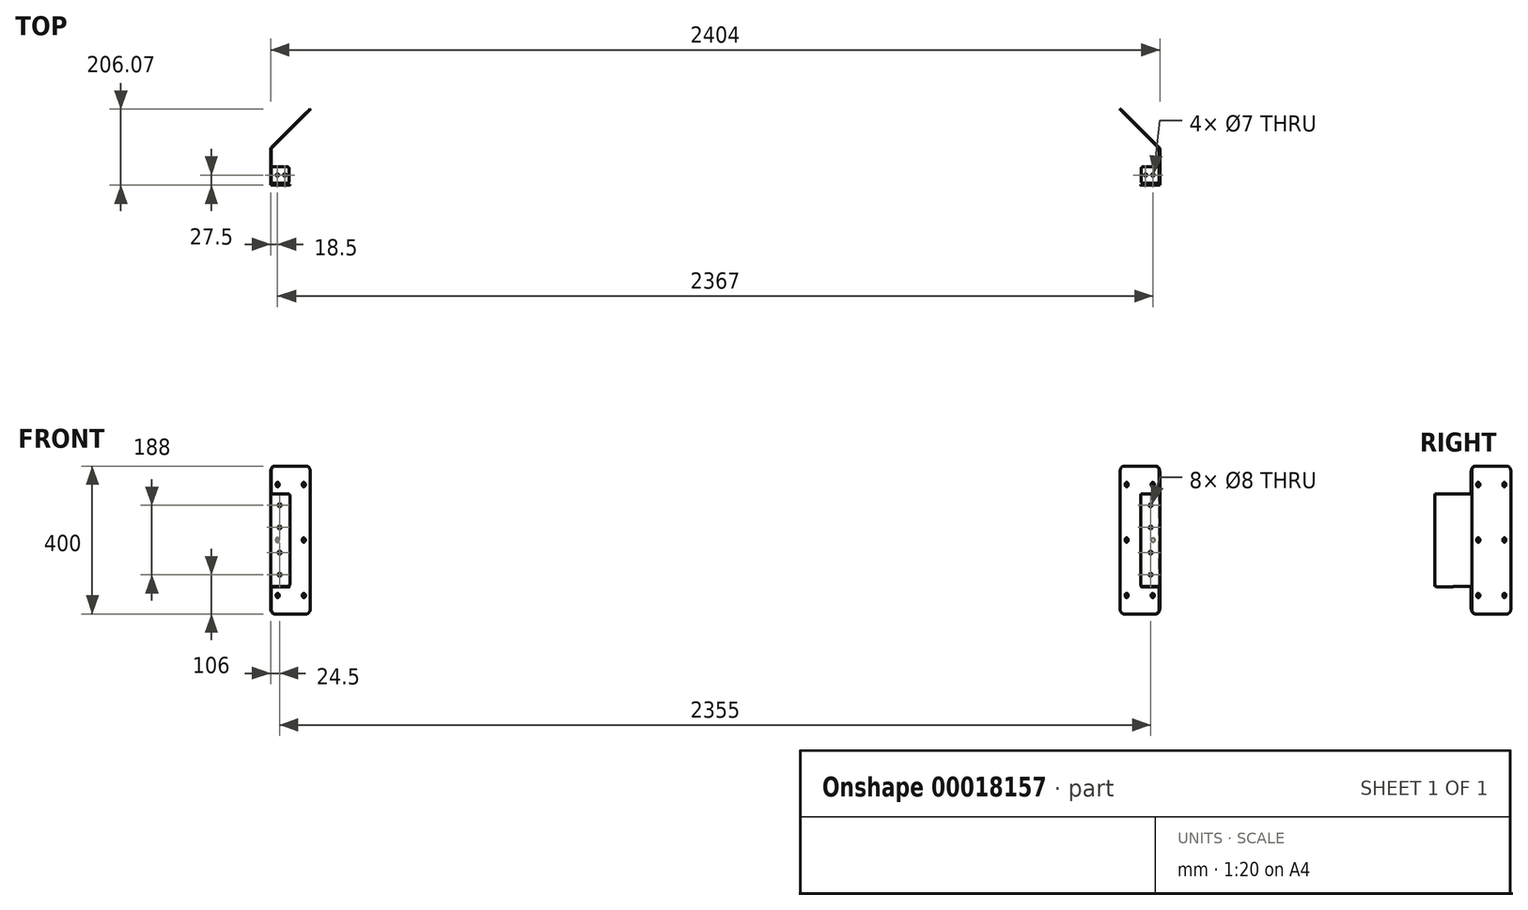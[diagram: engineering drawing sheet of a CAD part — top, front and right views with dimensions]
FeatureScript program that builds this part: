
annotation { "Feature Type Name" : "Feature", "Feature Type Description" : "" }
export const myFeature = defineFeature(function(context is Context, id is Id, definition is map)
    precondition{}
    {
        {
            var Q0;
            Q0=qCreatedBy(makeId("Front.planeOp"),FACE);
            var sketch = newSketch(context, id + "F0", { "sketchPlane" : qUnion([Q0])});
            skLineSegment(sketch, "E0.bottom", {"start": v(0, -125) * mm, "end": v(-45, -125) * mm});
            skLineSegment(sketch, "E0.top", {"start": v(0, 125) * mm, "end": v(-45, 125) * mm});
            skLineSegment(sketch, "E0.left", {"start": v(0, -125) * mm, "end": v(0, 125) * mm});
            skLineSegment(sketch, "E0.right", {"start": v(-50, -120) * mm, "end": v(-50, 120) * mm});
            skLineSegment(sketch, "E1", {"start": v(0, 0) * mm, "end": v(-144.9, 0) * mm, "construction": true});
            skPoint(sketch, "E2.visualSharp", {"position": v(-50, 125) * mm});
            skArc(sketch, "E2.filletArc", {"start": v(-45, 125) * mm, "mid": v(-48.54, 123.54) * mm, "end": v(-50, 120) * mm});
            skPoint(sketch, "E3.visualSharp", {"position": v(-50, -125) * mm});
            skArc(sketch, "E3.filletArc", {"start": v(-50, -120) * mm, "mid": v(-48.54, -123.54) * mm, "end": v(-45, -125) * mm});
            skLineSegment(sketch, "E4", {"start": v(-22.5, 125) * mm, "end": v(-22.5, -125) * mm, "construction": true});
            skCircle(sketch, "E5", {"center": v(-22.5, 34) * mm, "radius": 4 * mm});
            skCircle(sketch, "E6", {"center": v(-22.5, 94) * mm, "radius": 4 * mm});
            skCircle(sketch, "E7.MirrorC", {"center": v(-22.5, -34) * mm, "radius": 4 * mm});
            skCircle(sketch, "E8.MirrorC", {"center": v(-22.5, -94) * mm, "radius": 4 * mm});
            skSolve(sketch);
        }
        {
            var Q0;
            Q0 = qSketchRegion(id + "F0", true);
            extrude(context, id + "F1", {"entities" : qUnion([Q0]), "depth" : 2 * mm});
        }
        {
            var Q0;
            Q0=makeQuery(id+"F1.opExtrude","SWEPT_FACE",FACE,{"disambiguationData":[OSD([sQuery(id+"F0.wireOp",EDGE,"E0.left")])]});
            var sketch = newSketch(context, id + "F2", { "sketchPlane" : qUnion([Q0])});
            skLineSegment(sketch, "E9.bottom", {"start": v(-2, 125) * mm, "end": v(98, 125) * mm});
            skLineSegment(sketch, "E9.top", {"start": v(-2, -125) * mm, "end": v(98, -125) * mm});
            skLineSegment(sketch, "E9.left", {"start": v(-2, 125) * mm, "end": v(-2, -125) * mm});
            skLineSegment(sketch, "E9.right", {"start": v(98, 125) * mm, "end": v(98, -125) * mm});
            skSolve(sketch);
        }
        {
            var Q0;
            Q0 = qSketchRegion(id + "F2", true);
            extrude(context, id + "F3", {"entities" : qUnion([Q0]), "operationType" : NewBodyOperationType.ADD, "depth" : 2 * mm});
        }
        {
            var Q0;
            Q0=makeQuery(id+"F3.opExtrude","CAP_EDGE",EDGE,{"disambiguationData":[OSD([sQuery(id+"F2.wireOp",EDGE,"E9.right")])],"isStart":false});
            cPlane(context, id + "F4", {"entities" : qUnion([Q0]), "cplaneType" : CPlaneType.LINE_ANGLE, "offset" : 152.4 * mm, "angle" : 135 * degree, "width" : 152.4 * mm, "height" : 152.4 * mm});
        }
        {
            var Q0;
            Q0=qCreatedBy(id+"F4.planeOp",FACE);
            var sketch = newSketch(context, id + "F5", { "sketchPlane" : qUnion([Q0])});
            skLineSegment(sketch, "E10.bottom", {"start": v(82.88, 200) * mm, "end": v(202.88, 200) * mm});
            skLineSegment(sketch, "E10.top", {"start": v(82.88, -200) * mm, "end": v(202.88, -200) * mm});
            skLineSegment(sketch, "E10.left", {"start": v(67.88, 185) * mm, "end": v(67.88, -185) * mm});
            skLineSegment(sketch, "E10.right", {"start": v(217.88, 185) * mm, "end": v(217.88, -185) * mm});
            skPoint(sketch, "E11.visualSharp", {"position": v(67.88, 200) * mm});
            skArc(sketch, "E11.filletArc", {"start": v(82.88, 200) * mm, "mid": v(72.28, 195.6) * mm, "end": v(67.88, 185) * mm});
            skPoint(sketch, "E12.visualSharp", {"position": v(217.88, 200) * mm});
            skArc(sketch, "E12.filletArc", {"start": v(217.88, 185) * mm, "mid": v(213.49, 195.6) * mm, "end": v(202.88, 200) * mm});
            skPoint(sketch, "E13.visualSharp", {"position": v(217.88, -200) * mm});
            skArc(sketch, "E13.filletArc", {"start": v(202.88, -200) * mm, "mid": v(213.49, -195.6) * mm, "end": v(217.88, -185) * mm});
            skPoint(sketch, "E14.visualSharp", {"position": v(67.88, -200) * mm});
            skArc(sketch, "E14.filletArc", {"start": v(67.88, -185) * mm, "mid": v(72.28, -195.6) * mm, "end": v(82.88, -200) * mm});
            skLineSegment(sketch, "E15", {"start": v(142.88, 200) * mm, "end": v(142.88, -200) * mm, "construction": true});
            skLineSegment(sketch, "E16", {"start": v(217.88, 0) * mm, "end": v(67.88, 0) * mm, "construction": true});
            skLineSegment(sketch, "E17", {"start": v(192.88, 0) * mm, "end": v(192.88, 150) * mm, "construction": true});
            skCircle(sketch, "E18", {"center": v(192.88, 150) * mm, "radius": 6 * mm});
            skCircle(sketch, "E19", {"center": v(192.88, 0) * mm, "radius": 6 * mm});
            skCircle(sketch, "E20.MirrorC", {"center": v(192.88, -150) * mm, "radius": 6 * mm});
            skCircle(sketch, "E21.MirrorC", {"center": v(92.88, 150) * mm, "radius": 6 * mm});
            skCircle(sketch, "E22.MirrorC", {"center": v(92.88, 0) * mm, "radius": 6 * mm});
            skCircle(sketch, "E23.MirrorC", {"center": v(92.88, -150) * mm, "radius": 6 * mm});
            skSolve(sketch);
        }
        {
            var Q0;
            Q0 = qSketchRegion(id + "F5", true);
            extrude(context, id + "F6", {"entities" : qUnion([Q0]), "oppositeDirection" : true, "depth" : 2 * mm});
        }
        {
            var Q0;
            Q0=makeQuery(id+"F3.boolean.opBoolean","MERGE",FACE,{"derivedFrom":[makeQuery(id+"F1.opExtrude","SWEPT_FACE",FACE,{"disambiguationData":[OSD([sQuery(id+"F0.wireOp",EDGE,"E0.bottom")])]}),makeQuery(id+"F3.opExtrude","SWEPT_FACE",FACE,{"disambiguationData":[OSD([sQuery(id+"F2.wireOp",EDGE,"E9.top")])]})]});
            var sketch = newSketch(context, id + "F7", { "sketchPlane" : qUnion([Q0])});
            skLineSegment(sketch, "E24.bottom", {"start": v(2, -3) * mm, "end": v(-43, -3) * mm});
            skLineSegment(sketch, "E24.top", {"start": v(2, -48) * mm, "end": v(-43, -48) * mm});
            skLineSegment(sketch, "E24.left", {"start": v(2, -3) * mm, "end": v(2, -48) * mm});
            skLineSegment(sketch, "E24.right", {"start": v(-48, -8) * mm, "end": v(-48, -43) * mm});
            skPoint(sketch, "E25.visualSharp", {"position": v(-48, -3) * mm});
            skArc(sketch, "E25.filletArc", {"start": v(-43, -3) * mm, "mid": v(-46.54, -4.46) * mm, "end": v(-48, -8) * mm});
            skPoint(sketch, "E26.visualSharp", {"position": v(-48, -48) * mm});
            skArc(sketch, "E26.filletArc", {"start": v(-48, -43) * mm, "mid": v(-46.54, -46.54) * mm, "end": v(-43, -48) * mm});
            skCircle(sketch, "E27", {"center": v(-16.5, -25.5) * mm, "radius": 3.5 * mm});
            skCircle(sketch, "E28", {"center": v(-36.5, -25.5) * mm, "radius": 3.5 * mm});
            skLineSegment(sketch, "E29", {"start": v(-48, -25.5) * mm, "end": v(-7.46, -25.5) * mm, "construction": true});
            skSolve(sketch);
        }
        {
            var Q0;
            Q0 = qSketchRegion(id + "F7", true);
            extrude(context, id + "F8", {"entities" : qUnion([Q0]), "operationType" : NewBodyOperationType.ADD, "depth" : 2 * mm});
        }
        {
            var Q0;
            Q0=qCreatedBy(makeId("Right.planeOp"),FACE);
            cPlane(context, id + "F9", {"entities" : qUnion([Q0]), "cplaneType" : CPlaneType.OFFSET, "offset" : 1200 * mm, "oppositeDirection" : true, "width" : 152.4 * mm, "height" : 152.4 * mm});
        }
        {
            var Q0;
            Q0=makeQuery(id+"F1.opExtrude","SWEPT_BODY",BODY,{"disambiguationData":[OSD([sQuery(id+"F0.wireOp",EDGE,"E0.bottom"),sQuery(id+"F0.wireOp",EDGE,"E0.top"),sQuery(id+"F0.wireOp",EDGE,"E0.left"),sQuery(id+"F0.wireOp",EDGE,"E0.right"),sQuery(id+"F0.wireOp",EDGE,"E2.filletArc"),sQuery(id+"F0.wireOp",EDGE,"E3.filletArc")])]});
            var Q1;
            Q1=makeQuery(id+"F6.opExtrude","SWEPT_BODY",BODY,{"disambiguationData":[OSD([sQuery(id+"F5.wireOp",EDGE,"E10.bottom"),sQuery(id+"F5.wireOp",EDGE,"E10.top"),sQuery(id+"F5.wireOp",EDGE,"E10.left"),sQuery(id+"F5.wireOp",EDGE,"E10.right"),sQuery(id+"F5.wireOp",EDGE,"E11.filletArc"),sQuery(id+"F5.wireOp",EDGE,"E12.filletArc"),sQuery(id+"F5.wireOp",EDGE,"E13.filletArc"),sQuery(id+"F5.wireOp",EDGE,"E14.filletArc")])]});
            var Q2;
            Q2=qCreatedBy(id+"F9.planeOp",FACE);
            mirror(context, id + "F10", {"entities" : qUnion([Q0, Q1]), "mirrorPlane" : qUnion([Q2])});
        }
    });
